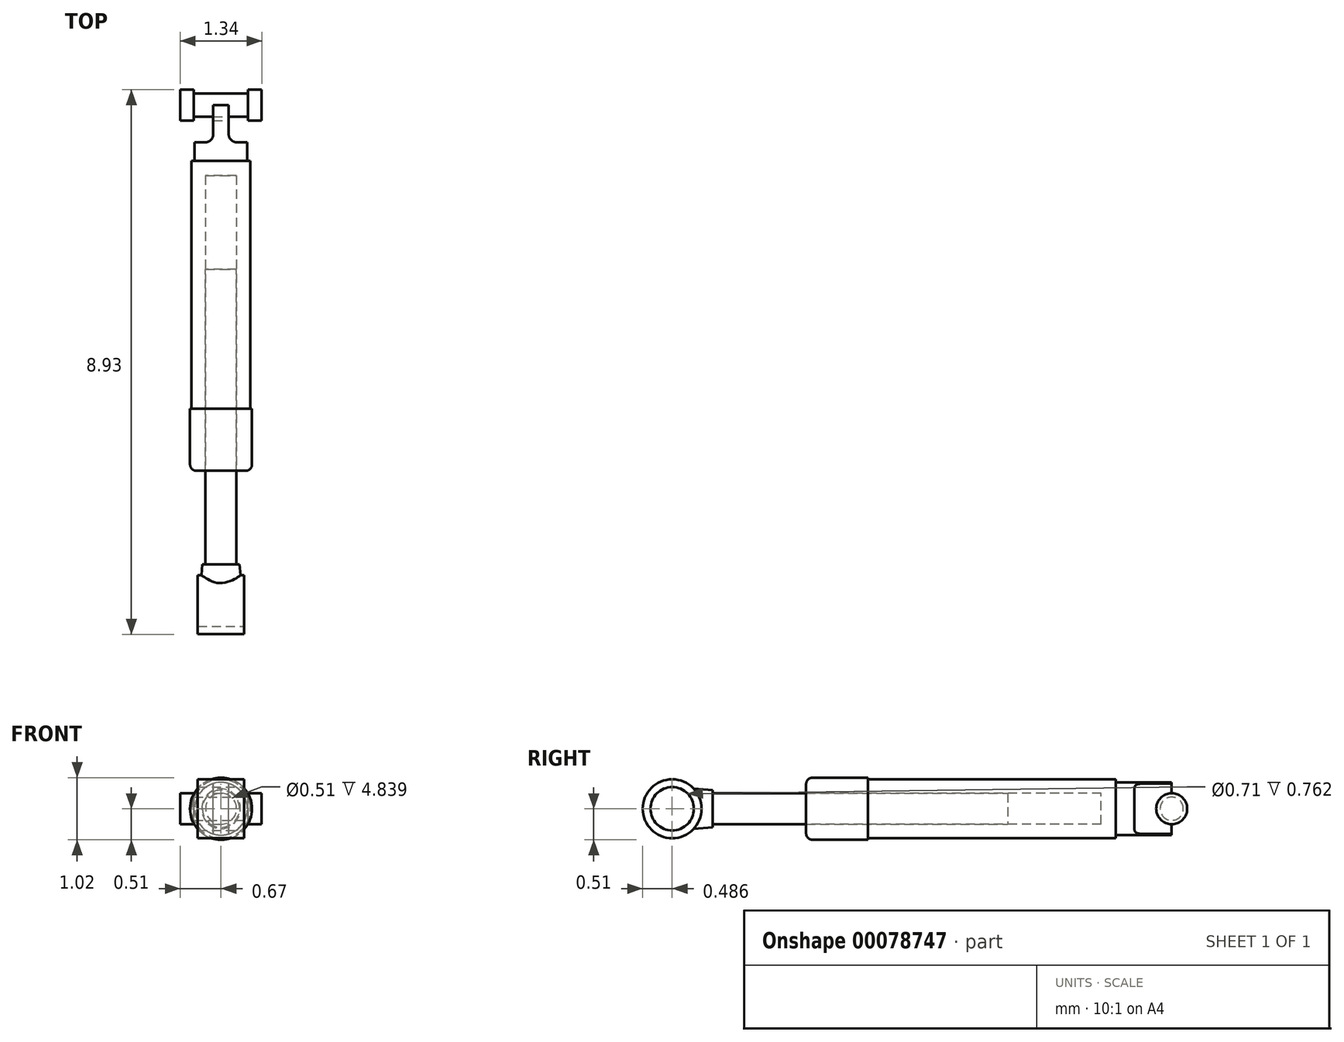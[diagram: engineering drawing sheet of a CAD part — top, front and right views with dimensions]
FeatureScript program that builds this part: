
annotation { "Feature Type Name" : "Feature", "Feature Type Description" : "" }
export const myFeature = defineFeature(function(context is Context, id is Id, definition is map)
    precondition{}
    {
        {
            var Q0;
            Q0=qCreatedBy(makeId("Right.planeOp"),FACE);
            var sketch = newSketch(context, id + "F0", { "sketchPlane" : qUnion([Q0])});
            skLineSegment(sketch, "E0", {"start": v(3.21, 0) * mm, "end": v(3.21, 0.48) * mm});
            skLineSegment(sketch, "E1", {"start": v(3.21, 0.48) * mm, "end": v(-0.85, 0.48) * mm});
            skLineSegment(sketch, "E2", {"start": v(-0.85, 0.48) * mm, "end": v(-0.85, 0.5) * mm});
            skLineSegment(sketch, "E3", {"start": v(-0.85, 0.5) * mm, "end": v(-1.87, 0.5) * mm});
            skLineSegment(sketch, "E4", {"start": v(-1.87, 0.5) * mm, "end": v(-1.87, 0.25) * mm});
            skLineSegment(sketch, "E5", {"start": v(-1.87, 0.25) * mm, "end": v(2.97, 0.25) * mm});
            skLineSegment(sketch, "E6", {"start": v(2.97, 0.25) * mm, "end": v(2.97, 0) * mm});
            skLineSegment(sketch, "E7", {"start": v(2.97, 0) * mm, "end": v(3.21, 0) * mm});
            skLineSegment(sketch, "E8", {"start": v(3.21, 0) * mm, "end": v(4.13, 0) * mm});
            skLineSegment(sketch, "E9", {"start": v(4.13, 0) * mm, "end": v(4.13, 0.43) * mm});
            skLineSegment(sketch, "E10", {"start": v(4.13, 0.43) * mm, "end": v(3.21, 0.43) * mm});
            skArc(sketch, "E11", {"start": v(4.13, 0.43) * mm, "mid": v(4.43, 0.3) * mm, "end": v(4.56, 0) * mm});
            skLineSegment(sketch, "E12", {"start": v(4.56, 0) * mm, "end": v(4.13, 0) * mm});
            skCircle(sketch, "E13", {"center": v(4.13, 0) * mm, "radius": 0.2 * mm});
            skSolve(sketch);
        }
        {
            var Q0;
            Q0=makeQuery(id+"F0.imprint","IMPRINT",FACE,{"disambiguationData":[TD([[makeQuery(id+"F0.imprint","IMPRINT",EDGE,{"derivedFrom":sQuery(id+"F0.wireOp",EDGE,"E0")}),1.0]])]});
            var Q1;
            {var subQ0=sQuery(id+"F0.wireOp",EDGE,"E8");Q1=makeQuery(id+"F0.imprint","IMPRINT",FACE,{"disambiguationData":[TD([[makeQuery(id+"F0.imprint","IMPRINT",EDGE,{"derivedFrom":subQ0}),1.0]])]});}
            var Q2;
            Q2=makeQuery(id+"F0.imprint","IMPRINT",FACE,{"disambiguationData":[TD([[makeQuery(id+"F0.imprint","IMPRINT",EDGE,{"derivedFrom":sQuery(id+"F0.wireOp",EDGE,"E9")}),-1.0]])]});
            var Q3;
            {var subQ0=sQuery(id+"F0.wireOp",EDGE,"E10");Q3=makeQuery(id+"F0.imprint","IMPRINT",FACE,{"disambiguationData":[TD([[makeQuery(id+"F0.imprint","IMPRINT",EDGE,{"derivedFrom":subQ0}),1.0]])]});}
            var Q4;
            {var subQ0=sQuery(id+"F0.wireOp",EDGE,"E11");Q4=makeQuery(id+"F0.imprint","IMPRINT",FACE,{"disambiguationData":[TD([[makeQuery(id+"F0.imprint","IMPRINT",EDGE,{"derivedFrom":subQ0}),-1.0]])]});}
            var Q5;
            Q5=sQuery(id+"F0.wireOp",EDGE,"E7");
            revolve(context, id + "F1", {"entities" : qUnion([Q0, Q1, Q2, Q3, Q4]), "axis" : qUnion([Q5]), "revolveType" : RevolveType.FULL});
        }
        {
            var Q0;
            Q0=makeQuery(id+"F1.opRevolve","SWEPT_EDGE",EDGE,{"disambiguationData":[OSD([sQuery(id+"F0.wireOp",EDGE,"E3"),sQuery(id+"F0.wireOp",EDGE,"E4")])]});
            fillet(context, id + "F2", {"entities" : qUnion([Q0]), "radius" : 0.1 * mm, "tangentPropagation" : true, "allowEdgeOverflow" : false});
        }
        {
            var Q0;
            Q0=qCreatedBy(makeId("Top.planeOp"),FACE);
            var sketch = newSketch(context, id + "F3", { "sketchPlane" : qUnion([Q0])});
            skLineSegment(sketch, "E14", {"start": v(0, 0) * mm, "end": v(0, 7.15) * mm, "construction": true});
            skLineSegment(sketch, "E15.bottom", {"start": v(0.13, 4.79) * mm, "end": v(0.64, 4.79) * mm});
            skLineSegment(sketch, "E15.top", {"start": v(0.13, 3.52) * mm, "end": v(0.64, 3.52) * mm});
            skLineSegment(sketch, "E15.left", {"start": v(0.13, 4.79) * mm, "end": v(0.13, 3.52) * mm});
            skLineSegment(sketch, "E15.right", {"start": v(0.64, 4.79) * mm, "end": v(0.64, 3.52) * mm});
            skLineSegment(sketch, "E16.MirrorCS", {"start": v(-0.13, 4.79) * mm, "end": v(-0.13, 3.52) * mm});
            skLineSegment(sketch, "E17.MirrorCS", {"start": v(-0.13, 3.52) * mm, "end": v(-0.64, 3.52) * mm});
            skLineSegment(sketch, "E18.MirrorCS", {"start": v(-0.64, 4.79) * mm, "end": v(-0.64, 3.52) * mm});
            skLineSegment(sketch, "E19.MirrorCS", {"start": v(-0.13, 4.79) * mm, "end": v(-0.64, 4.79) * mm});
            skSolve(sketch);
        }
        {
            var Q0;
            Q0=makeQuery(id+"F3.imprint","IMPRINT",FACE,{"disambiguationData":[TD([[makeQuery(id+"F3.imprint","IMPRINT",EDGE,{"derivedFrom":sQuery(id+"F3.wireOp",EDGE,"E16.MirrorCS")}),-1.0]])]});
            var Q1;
            Q1=makeQuery(id+"F3.imprint","IMPRINT",FACE,{"disambiguationData":[TD([[makeQuery(id+"F3.imprint","IMPRINT",EDGE,{"derivedFrom":sQuery(id+"F3.wireOp",EDGE,"E15.bottom")}),-1.0]])]});
            extrude(context, id + "F4", {"entities" : qUnion([Q0, Q1]), "operationType" : NewBodyOperationType.REMOVE, "oppositeDirection" : true, "depth" : 2.54 * mm, "symmetric" : true});
        }
        {
            var Q0;
            Q0=makeQuery(id+"F4.boolean.opBoolean","COPY",EDGE,{"derivedFrom":makeQuery(id+"F4.opExtrude","SWEPT_EDGE",EDGE,{"disambiguationData":[OSD([sQuery(id+"F3.wireOp",EDGE,"E16.MirrorCS"),sQuery(id+"F3.wireOp",EDGE,"E17.MirrorCS")])]})});
            var Q1;
            Q1=makeQuery(id+"F4.boolean.opBoolean","COPY",EDGE,{"derivedFrom":makeQuery(id+"F4.opExtrude","SWEPT_EDGE",EDGE,{"disambiguationData":[OSD([sQuery(id+"F3.wireOp",EDGE,"E15.top"),sQuery(id+"F3.wireOp",EDGE,"E15.left")])]})});
            fillet(context, id + "F5", {"entities" : qUnion([Q0, Q1]), "radius" : 0.13 * mm, "tangentPropagation" : true, "allowEdgeOverflow" : false});
        }
        {
            var Q0;
            {var subQ0=sQuery(id+"F0.wireOp",EDGE,"E12");var subQ3=sQuery(id+"F0.wireOp",EDGE,"E13");var subQ5=makeQuery(id+"F0.imprint","INTERSECT",VERTEX,{"derivedFrom":[subQ0,subQ3]});Q0=makeQuery(id+"F0.imprint","IMPRINT",FACE,{"disambiguationData":[TD([[makeQuery(id+"F0.imprint","IMPRINT",EDGE,{"disambiguationData":[TD([[subQ5,-1.0]])],"derivedFrom":subQ3}),1.0]])]});}
            var Q1;
            {var subQ1=sQuery(id+"F0.wireOp",EDGE,"E8");var subQ3=sQuery(id+"F0.wireOp",EDGE,"E13");var subQ4=makeQuery(id+"F0.imprint","INTERSECT",VERTEX,{"derivedFrom":[subQ1,subQ3]});Q1=makeQuery(id+"F0.imprint","IMPRINT",FACE,{"disambiguationData":[TD([[makeQuery(id+"F0.imprint","IMPRINT",EDGE,{"disambiguationData":[TD([[subQ4,1.0]])],"derivedFrom":subQ3}),1.0]])]});}
            var Q2;
            {var subQ1=sQuery(id+"F0.wireOp",EDGE,"E8");var subQ3=sQuery(id+"F0.wireOp",EDGE,"E13");var subQ4=makeQuery(id+"F0.imprint","INTERSECT",VERTEX,{"derivedFrom":[subQ1,subQ3]});Q2=makeQuery(id+"F0.imprint","IMPRINT",FACE,{"disambiguationData":[TD([[makeQuery(id+"F0.imprint","IMPRINT",EDGE,{"disambiguationData":[TD([[subQ4,-1.0]])],"derivedFrom":subQ3}),1.0]])]});}
            extrude(context, id + "F6", {"entities" : qUnion([Q0, Q1, Q2]), "operationType" : NewBodyOperationType.REMOVE, "oppositeDirection" : true, "depth" : 25.4 * mm, "symmetric" : true});
        }
        {
            var Q0;
            Q0=qCreatedBy(makeId("Right.planeOp"),FACE);
            var sketch = newSketch(context, id + "F7", { "sketchPlane" : qUnion([Q0])});
            skCircle(sketch, "E20", {"center": v(-4.06, 0) * mm, "radius": 0.48 * mm});
            skLineSegment(sketch, "E21.bottom", {"start": v(1.44, 0) * mm, "end": v(-3.4, 0) * mm});
            skLineSegment(sketch, "E21.top", {"start": v(1.44, 0.25) * mm, "end": v(-3.4, 0.25) * mm});
            skLineSegment(sketch, "E21.left", {"start": v(1.44, 0) * mm, "end": v(1.44, 0.25) * mm});
            skLineSegment(sketch, "E21.right", {"start": v(-3.4, 0) * mm, "end": v(-3.4, 0.25) * mm});
            skCircle(sketch, "E22", {"center": v(-4.06, 0) * mm, "radius": 0.36 * mm});
            skLineSegment(sketch, "E23", {"start": v(-3.4, 0.25) * mm, "end": v(-3.4, 0.3) * mm});
            skLineSegment(sketch, "E24", {"start": v(-3.4, 0.3) * mm, "end": v(-4.04, 0.35) * mm});
            skLineSegment(sketch, "E25", {"start": v(-3.4, 0) * mm, "end": v(-3.7, 0) * mm});
            skSolve(sketch);
        }
        {
            var Q0;
            {var subQ0=sQuery(id+"F7.wireOp",EDGE,"E22");var subQ1=makeQuery(id+"F7.imprint","INTERSECT",VERTEX,{"derivedFrom":[subQ0,sQuery(id+"F7.wireOp",EDGE,"E24")]});Q0=makeQuery(id+"F7.imprint","IMPRINT",FACE,{"disambiguationData":[TD([[makeQuery(id+"F7.imprint","IMPRINT",EDGE,{"disambiguationData":[TD([[subQ1,1.0]])],"derivedFrom":subQ0}),1.0]])]});}
            var Q1;
            {var subQ0=sQuery(id+"F7.wireOp",EDGE,"E24");var subQ1=sQuery(id+"F7.wireOp",EDGE,"E20");var subQ2=makeQuery(id+"F7.imprint","INTERSECT",VERTEX,{"derivedFrom":[subQ1,subQ0]});Q1=makeQuery(id+"F7.imprint","IMPRINT",FACE,{"disambiguationData":[TD([[makeQuery(id+"F7.imprint","IMPRINT",EDGE,{"disambiguationData":[TD([[subQ2,1.0]])],"derivedFrom":subQ1}),1.0]])]});}
            var Q2;
            {var subQ0=sQuery(id+"F7.wireOp",EDGE,"E24");var subQ1=sQuery(id+"F7.wireOp",EDGE,"E20");var subQ2=makeQuery(id+"F7.imprint","INTERSECT",VERTEX,{"derivedFrom":[subQ1,subQ0]});Q2=makeQuery(id+"F7.imprint","IMPRINT",FACE,{"disambiguationData":[TD([[makeQuery(id+"F7.imprint","IMPRINT",EDGE,{"disambiguationData":[TD([[subQ2,-1.0]])],"derivedFrom":subQ1}),1.0]])]});}
            extrude(context, id + "F8", {"entities" : qUnion([Q0, Q1, Q2]), "depth" : 0.76 * mm, "symmetric" : true});
        }
        {
            var Q0;
            {var subQ6=sQuery(id+"F7.wireOp",EDGE,"E21.right");Q0=makeQuery(id+"F7.imprint","IMPRINT",FACE,{"disambiguationData":[TD([[makeQuery(id+"F7.imprint","IMPRINT",EDGE,{"derivedFrom":subQ6}),1.0]])]});}
            var Q1;
            {var subQ0=sQuery(id+"F7.wireOp",EDGE,"E24");var subQ1=sQuery(id+"F7.wireOp",EDGE,"E20");var subQ2=makeQuery(id+"F7.imprint","INTERSECT",VERTEX,{"derivedFrom":[subQ1,subQ0]});Q1=makeQuery(id+"F7.imprint","IMPRINT",FACE,{"disambiguationData":[TD([[makeQuery(id+"F7.imprint","IMPRINT",EDGE,{"disambiguationData":[TD([[subQ2,1.0]])],"derivedFrom":subQ1}),1.0]])]});}
            var Q2;
            Q2=sQuery(id+"F7.wireOp",EDGE,"E25");
            revolve(context, id + "F9", {"operationType" : NewBodyOperationType.ADD, "entities" : qUnion([Q0, Q1]), "axis" : qUnion([Q2]), "revolveType" : RevolveType.FULL});
        }
        {
            var Q0;
            {var subQ0=sQuery(id+"F7.wireOp",EDGE,"E22");var subQ1=makeQuery(id+"F7.imprint","INTERSECT",VERTEX,{"derivedFrom":[subQ0,sQuery(id+"F7.wireOp",EDGE,"E24")]});Q0=makeQuery(id+"F7.imprint","IMPRINT",FACE,{"disambiguationData":[TD([[makeQuery(id+"F7.imprint","IMPRINT",EDGE,{"disambiguationData":[TD([[subQ1,1.0]])],"derivedFrom":subQ0}),1.0]])]});}
            extrude(context, id + "F10", {"entities" : qUnion([Q0]), "operationType" : NewBodyOperationType.REMOVE, "oppositeDirection" : true, "depth" : 25.4 * mm, "symmetric" : true});
        }
        {
            var Q0;
            Q0=makeQuery(id+"F7.imprint","IMPRINT",FACE,{"disambiguationData":[TD([[makeQuery(id+"F7.imprint","IMPRINT",EDGE,{"derivedFrom":sQuery(id+"F7.wireOp",EDGE,"E21.bottom")}),-1.0]])]});
            var Q1;
            Q1=sQuery(id+"F7.wireOp",EDGE,"E21.bottom");
            revolve(context, id + "F11", {"entities" : qUnion([Q0]), "axis" : qUnion([Q1]), "revolveType" : RevolveType.FULL});
        }
        {
            var Q0;
            Q0=qCreatedBy(makeId("Right.planeOp"),FACE);
            var sketch = newSketch(context, id + "F12", { "sketchPlane" : qUnion([Q0])});
            skCircle(sketch, "E26.0", {"center": v(4.13, 0) * mm, "radius": 0.2 * mm});
            skCircle(sketch, "E27", {"center": v(4.13, 0) * mm, "radius": 0.25 * mm});
            skSolve(sketch);
        }
        {
            var Q0;
            Q0=makeQuery(id+"F12.imprint","IMPRINT",FACE,{"disambiguationData":[TD([[makeQuery(id+"F12.imprint","IMPRINT",EDGE,{"derivedFrom":sQuery(id+"F12.wireOp",EDGE,"E26.0")}),1.0]])]});
            var Q1;
            Q1=makeQuery(id+"F12.imprint","IMPRINT",FACE,{"disambiguationData":[TD([[makeQuery(id+"F12.imprint","IMPRINT",EDGE,{"derivedFrom":sQuery(id+"F12.wireOp",EDGE,"E26.0")}),-1.0]])]});
            extrude(context, id + "F13", {"entities" : qUnion([Q0, Q1]), "depth" : 1.33 * mm, "symmetric" : true});
        }
        {
            var Q0;
            Q0=makeQuery(id+"F12.imprint","IMPRINT",FACE,{"disambiguationData":[TD([[makeQuery(id+"F12.imprint","IMPRINT",EDGE,{"derivedFrom":sQuery(id+"F12.wireOp",EDGE,"E26.0")}),-1.0]])]});
            extrude(context, id + "F14", {"entities" : qUnion([Q0]), "operationType" : NewBodyOperationType.REMOVE, "oppositeDirection" : true, "depth" : 0.89 * mm, "symmetric" : true});
        }
    });
